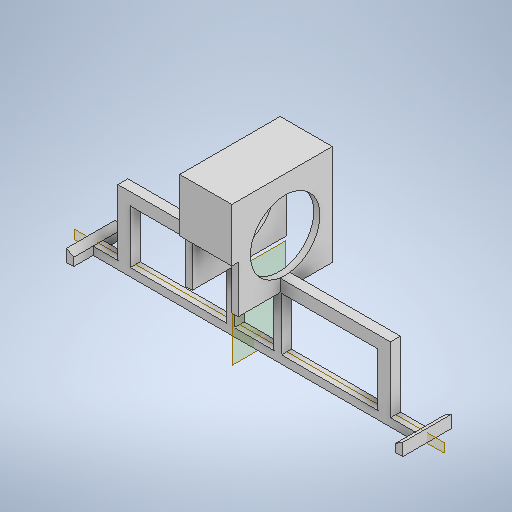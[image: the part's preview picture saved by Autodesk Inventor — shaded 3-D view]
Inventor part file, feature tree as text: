
AUTODESK INVENTOR PART (.ipt)
format: ipt  version: 2025.1 (Build 291241000, 241)  size: 388,608 bytes
history: native  units: mm
features: extrude x10, sketch x10, plane x2
ambient origin geometry x8: Origin, YZ Plane, XZ Plane, XY Plane, X Axis, Y Axis, Z Axis, Center Point
bodies: Volumenkörper1 (feature_tree)
feature tree (22):
  extrude  "Extrusion1"  Depth=2.85mm
  plane  "Arbeitsebene1"
  extrude  "Extrusion2"  Depth=2.85mm
  extrude  "Extrusion7"  Depth=10.0mm
  extrude  "Extrusion8"  Depth=26.5mm TaperAngle=0.0deg
  plane  "Arbeitsebene2"
  extrude  "Extrusion9"  Depth=15.0mm
  extrude  "Extrusion19"  Depth=14.0mm TaperAngle=0.0deg
  extrude  "Extrusion20"  Depth=16.0mm TaperAngle=0.0deg
  extrude  "Extrusion21"  Depth=2.5mm TaperAngle=0.0deg
  extrude  "Extrusion22"  Depth=2.5mm
  extrude  "Extrusion23"  Depth=2.5mm
  sketch  "Skizze1"  dims[d0=135.6mm d1=4.0mm d2=3.25mm d3=0.0mm d4=2.85mm]
  sketch  "Skizze2"  dims[d5=1.75mm d6=2.85mm]
  sketch  "Skizze7"  dims[d7=19.7mm d8=0.0mm d27=10.0mm]
  sketch  "Skizze8"  dims[d28=10.0mm d29=26.5mm d30=0.0mm]
  sketch  "Skizze9"  dims[d31=15.0mm d32=15.0mm]
  sketch  "Skizze17"  dims[d33=21.5mm d34=0.0mm d35=14.0mm d36=0.0mm]
  sketch  "Skizze19"  dims[d71=21.0mm d72=0.0mm d73=16.0mm d74=0.0mm]
  sketch  "Skizze20"  dims[d75=2.5mm d76=0.0mm d77=2.5mm d78=0.0mm]
  sketch  "Skizze21"  dims[d79=2.5mm d80=0.0mm]
  sketch  "Skizze22"  dims[d81=3.0mm d82=2.5mm d83=3.0mm d84=2.5mm d85=0.0mm d15=0.5mm d16=0.872665mm d17=0.5mm d18=0.872665mm d67=0.5mm d68=0.872665mm d69=0.5mm d70=0.872665mm]
